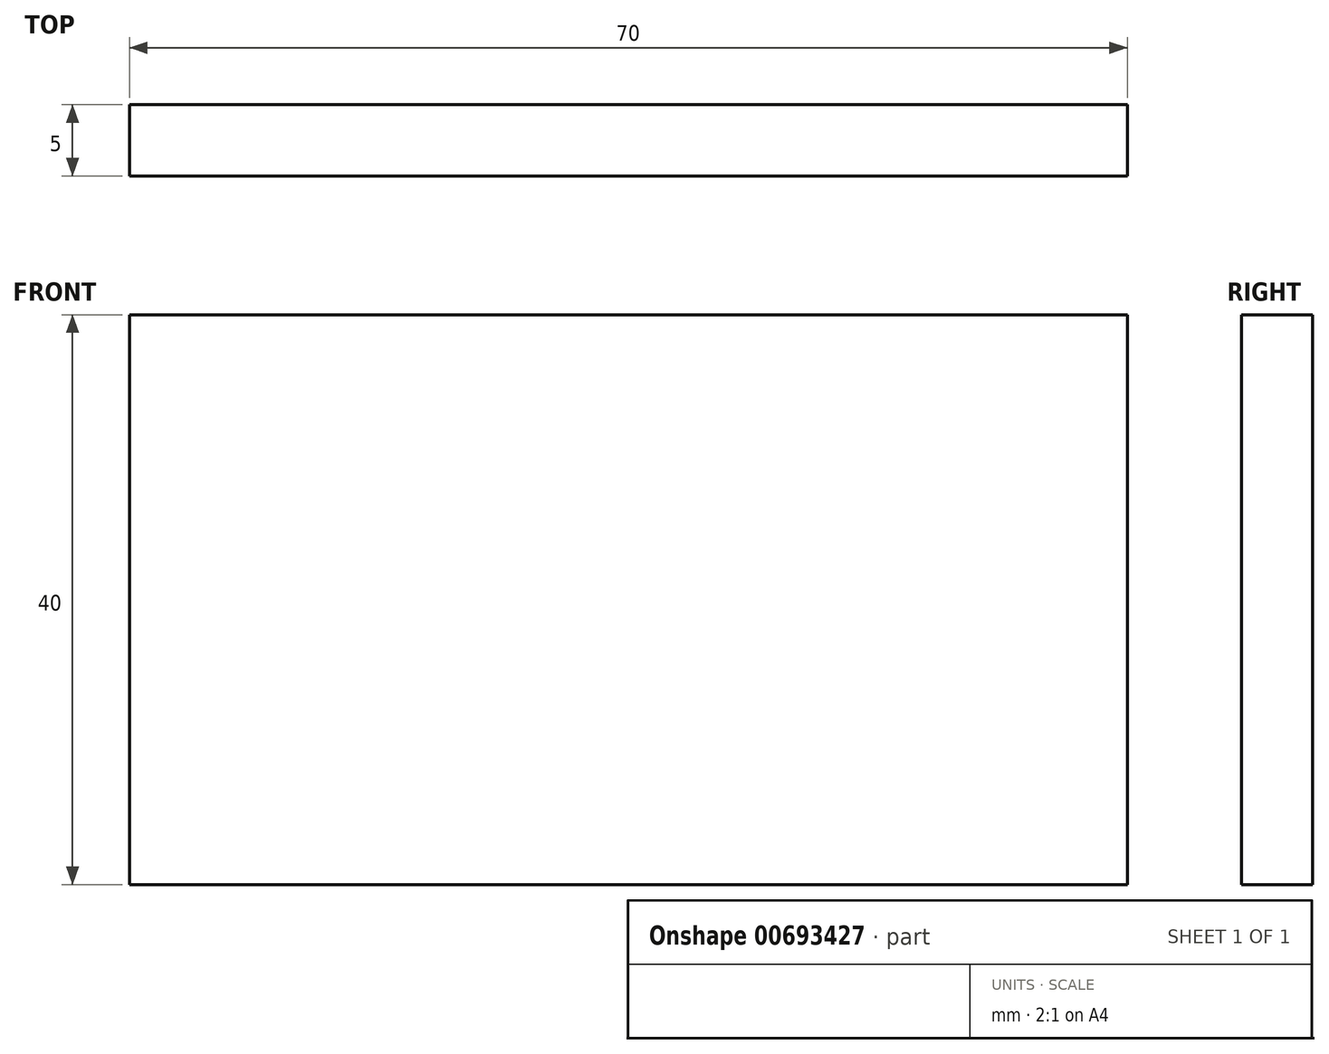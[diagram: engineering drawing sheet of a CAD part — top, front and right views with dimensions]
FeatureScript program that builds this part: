
annotation { "Feature Type Name" : "Feature", "Feature Type Description" : "" }
export const myFeature = defineFeature(function(context is Context, id is Id, definition is map)
    precondition{}
    {
        {
            var Q0;
            Q0=qCreatedBy(makeId("Front.planeOp"),FACE);
            var sketch = newSketch(context, id + "F0", { "sketchPlane" : qUnion([Q0])});
            skLineSegment(sketch, "E0.bottom", {"start": v(0, 0) * mm, "end": v(70, 0) * mm});
            skLineSegment(sketch, "E0.top", {"start": v(0, 40) * mm, "end": v(70, 40) * mm});
            skLineSegment(sketch, "E0.left", {"start": v(0, 0) * mm, "end": v(0, 40) * mm});
            skLineSegment(sketch, "E0.right", {"start": v(70, 0) * mm, "end": v(70, 40) * mm});
            skSolve(sketch);
        }
        {
            var Q0;
            Q0 = qSketchRegion(id + "F0", true);
            extrude(context, id + "F1", {"entities" : qUnion([Q0]), "depth" : 5 * mm, "offsetDistance" : 25.4 * mm});
        }
    });
